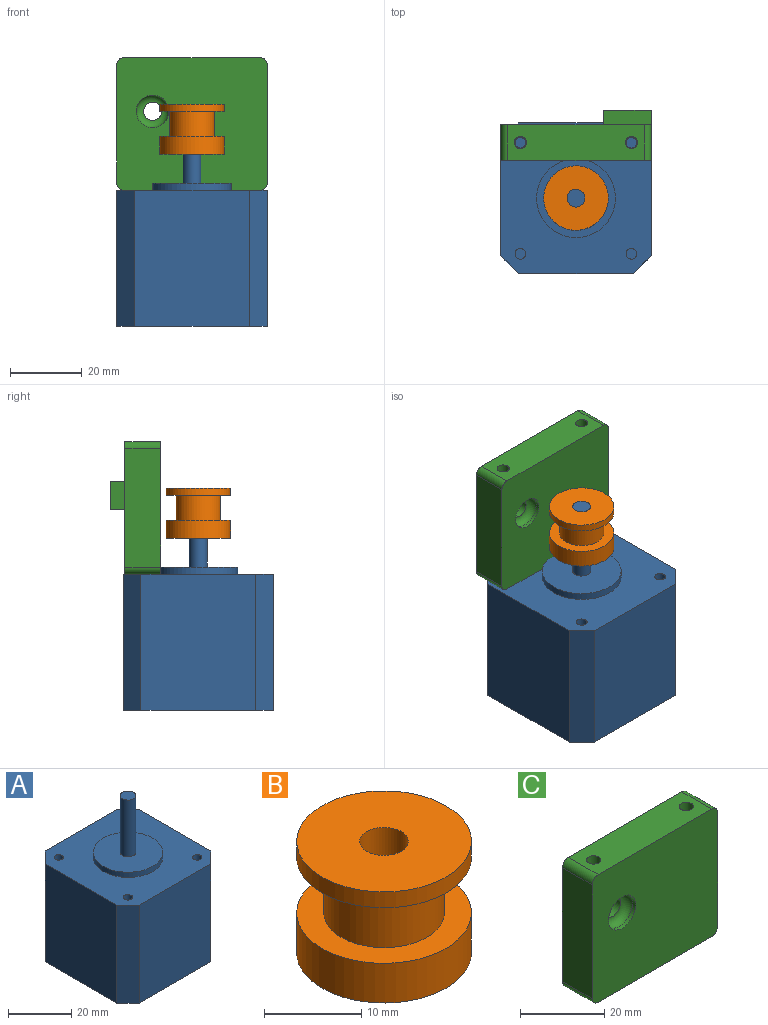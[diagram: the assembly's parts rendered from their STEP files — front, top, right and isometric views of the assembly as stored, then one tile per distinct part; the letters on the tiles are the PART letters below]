
ASSEMBLY  parts=3 mates=2
PART A: 22 faces, bbox 42x42x62 mm
  f0: plane 38x32mm, normal (-1,0,0), area 1216mm2, adj f4,f5,f8,f9
  f1: plane 38x32mm, normal (0,-1,0), area 1216mm2, adj f4,f5,f7,f9
  f2: plane 38x32mm, normal (1,0,0), area 1216mm2, adj f4,f5,f6,f7
  f3: plane 38x32mm, normal (0,1,0), area 1216mm2, adj f4,f5,f6,f8
  f4: plane 42x42mm, normal (0,0,1), area 1305.6mm2, adj f0,f1,f2,f3,f6,f7,f8,f9
  f5: plane 42x42mm, normal (0,0,-1), area 1714mm2, adj f0,f1,f2,f3,f6,f7,f8,f9
  f6: plane 38x5mm, normal (0.71,0.71,0), area 268.7mm2, adj f2,f3,f4,f5
  f7: plane 38x5mm, normal (0.71,-0.71,0), area 268.7mm2, adj f1,f2,f4,f5
  f8: plane 38x5mm, normal (-0.71,0.71,0), area 268.7mm2, adj f0,f3,f4,f5
  f9: plane 38x5mm, normal (-0.71,-0.71,0), area 268.7mm2, adj f0,f1,f4,f5
  f10: cylinder r=11mm len=22mm, axis (0,0,-1), area 138.2mm2, adj f4,f11
  f11: plane 22x22mm, normal (0,0,1), area 360.5mm2, adj f10,f12
  f12: cylinder r=2.5mm len=22mm, axis (0,0,-1), area 345.6mm2, adj f11,f13
  f13: plane 5x5mm, normal (0,0,1), area 19.6mm2, adj f12
  f14: cylinder r=1.5mm len=25mm, axis (0,0,1), area 235.6mm2, adj f4,f15
  f15: plane 3x3mm, normal (0,0,1), area 7.1mm2, adj f14
  f16: cylinder r=1.5mm len=25mm, axis (0,0,1), area 235.6mm2, adj f4,f17
  f17: plane 3x3mm, normal (0,0,1), area 7.1mm2, adj f16
  f18: cylinder r=1.5mm len=25mm, axis (0,0,1), area 235.6mm2, adj f4,f19
  f19: plane 3x3mm, normal (0,0,1), area 7.1mm2, adj f18
  f20: cylinder r=1.5mm len=25mm, axis (0,0,1), area 235.6mm2, adj f4,f21
  f21: plane 3x3mm, normal (0,0,1), area 7.1mm2, adj f20
PART B: 8 faces, bbox 18x18x14 mm
  f0: cylinder r=9mm len=18mm, axis (0,0,-1), area 282.7mm2, adj f1,f2
  f1: plane 18x18mm, normal (0,0,1), area 133.7mm2, adj f0,f3
  f2: plane 18x18mm, normal (0,0,-1), area 234.8mm2, adj f0,f7
  f3: cylinder r=6.2mm len=12.4mm, axis (0,0,-1), area 272.7mm2, adj f1,f6
  f4: cylinder r=9mm len=18mm, axis (0,0,-1), area 113.1mm2, adj f5,f6
  f5: plane 18x18mm, normal (0,0,1), area 234.8mm2, adj f4,f7
  f6: plane 18x18mm, normal (0,0,-1), area 133.7mm2, adj f3,f4
  f7: cylinder r=2.5mm len=14mm, axis (0,0,1), area 219.9mm2, adj f2,f5
PART C: 19 faces, bbox 42x14.4x37 mm
  f0: cylinder r=2.55mm len=7mm, axis (0,1,0), area 112.2mm2, adj f1,f14
  f1: plane 42x37mm, normal (0,1,0), area 1423.6mm2, adj f0,f2,f4,f5,f6,f9,f10,f11
  f2: plane 33x10mm, normal (-1,0,0), area 330mm2, adj f1,f3,f15,f17
  f3: plane 42x37mm, normal (0,-1,0), area 1485.5mm2, adj f2,f4,f5,f6,f13,f15,f16,f17
  f4: plane 33x14mm, normal (1,0,0), area 362mm2, adj f1,f3,f9,f11,f12,f16,f18
  f5: plane 38x10mm, normal (0,0,1), area 361.8mm2, adj f1,f3,f7,f8,f17,f18
  f6: plane 38x10mm, normal (0,0,-1), area 361.8mm2, adj f1,f3,f7,f8,f15,f16
  f7: cylinder r=1.7mm len=37mm, axis (0,0,1), area 395.2mm2, adj f5,f6
  f8: cylinder r=1.7mm len=37mm, axis (0,0,1), area 395.2mm2, adj f5,f6
  f9: plane 13.31x4mm, normal (0,0,-1), area 53.3mm2, adj f1,f4,f10,f12
  f10: plane 8x4mm, normal (-1,0,0), area 32mm2, adj f1,f9,f11,f12
  f11: plane 13.31x4mm, normal (0,0,1), area 53.3mm2, adj f1,f4,f10,f12
  f12: plane 13.31x8mm, normal (0,1,0), area 106.5mm2, adj f4,f9,f10,f11
  f13: cylinder r=4.55mm len=9.1mm, axis (0,-1,0), area 28.6mm2, adj f3,f14
  f14: torus R=2.55mm, axis (0,-1,0), area 75.5mm2, adj f0,f13
  f15: cylinder r=2mm len=10mm, axis (0,-1,0), area 31.4mm2, adj f1,f2,f3,f6
  f16: cylinder r=2mm len=10mm, axis (0,1,0), area 31.4mm2, adj f1,f3,f4,f6
  f17: cylinder r=2mm len=10mm, axis (0,1,0), area 31.4mm2, adj f1,f2,f3,f5
  f18: cylinder r=2mm len=10mm, axis (0,-1,0), area 31.4mm2, adj f1,f3,f4,f5
PLACE A t=(-19.22,-27.33,-36.28)mm
PLACE B t=(1.78,-6.33,11.72)mm
PLACE C t=(-2.36,4.17,1.72)mm
MATE fastened A.f20 <-> C.f7  axis (0,0,1) through (-13.72,9.17,1.72)mm
MATE fastened B.f0 <-> A.f10  axis (0,0,1) through (1.78,-6.33,25.72)mm
